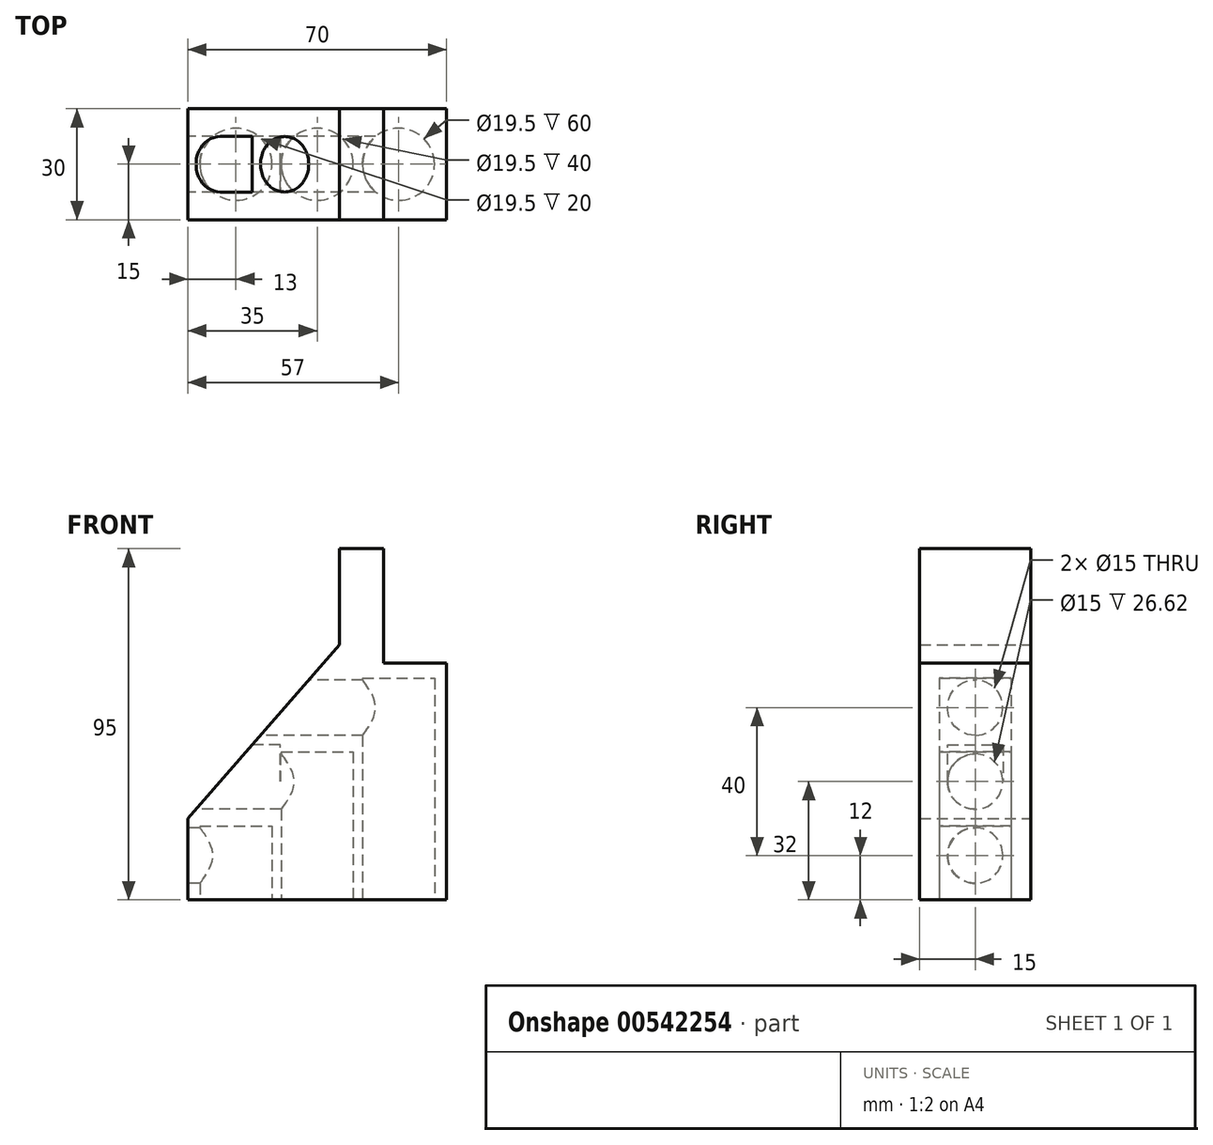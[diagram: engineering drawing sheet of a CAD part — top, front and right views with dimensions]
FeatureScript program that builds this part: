
annotation { "Feature Type Name" : "Feature", "Feature Type Description" : "" }
export const myFeature = defineFeature(function(context is Context, id is Id, definition is map)
    precondition{}
    {
        {
            var Q0;
            Q0=qCreatedBy(makeId("Top.planeOp"),FACE);
            var sketch = newSketch(context, id + "F0", { "sketchPlane" : qUnion([Q0])});
            skLineSegment(sketch, "E0.direction1", {"start": v(0, 0) * mm, "end": v(22, 0) * mm, "construction": true});
            skLineSegment(sketch, "E1.bottom", {"start": v(-13, 15) * mm, "end": v(57, 15) * mm});
            skLineSegment(sketch, "E1.top", {"start": v(-13, -15) * mm, "end": v(57, -15) * mm});
            skLineSegment(sketch, "E1.left", {"start": v(-13, 15) * mm, "end": v(-13, -15) * mm});
            skLineSegment(sketch, "E1.right", {"start": v(57, 15) * mm, "end": v(57, -15) * mm});
            skSolve(sketch);
        }
        {
            var Q0;
            Q0 = qSketchRegion(id + "F0", true);
            var Q1;
            Q1=makeQuery(id+"F0.imprint","IMPRINT",FACE,{"disambiguationData":[TD([[makeQuery(id+"F0.imprint","IMPRINT",EDGE,{"derivedFrom":sQuery(id+"F0.wireOp",EDGE,"SlxlytLZ-BfXm-e8RE-Wzol-MLgFMUTTCqxw")}),1.0]])]});
            var Q2;
            Q2=makeQuery(id+"F0.imprint","IMPRINT",FACE,{"disambiguationData":[TD([[makeQuery(id+"F0.imprint","IMPRINT",EDGE,{"derivedFrom":sQuery(id+"F0.wireOp",EDGE,"E0.1.0.0")}),1.0]])]});
            var Q3;
            Q3=makeQuery(id+"F0.imprint","IMPRINT",FACE,{"disambiguationData":[TD([[makeQuery(id+"F0.imprint","IMPRINT",EDGE,{"derivedFrom":sQuery(id+"F0.wireOp",EDGE,"E0.2.0.0")}),1.0]])]});
            extrude(context, id + "F1", {"entities" : qUnion([Q0, Q1, Q2, Q3]), "depth" : 95 * mm, "offsetDistance" : 25 * mm});
        }
        {
            var Q0;
            Q0=makeQuery(id+"F1.opExtrude","SWEPT_FACE",FACE,{"disambiguationData":[OSD([sQuery(id+"F0.wireOp",EDGE,"E1.top")])]});
            var sketch = newSketch(context, id + "F2", { "sketchPlane" : qUnion([Q0])});
            skLineSegment(sketch, "E2", {"start": v(40, 95) * mm, "end": v(40, 64) * mm});
            skLineSegment(sketch, "E3", {"start": v(40, 64) * mm, "end": v(57, 64) * mm});
            skSolve(sketch);
        }
        {
            var Q0;
            Q0 = qSketchRegion(id + "F2", true);
            var Q1;
            {var subQ0=sQuery(id+"F2.wireOp",EDGE,"E2");Q1=makeQuery(id+"F2.imprint","IMPRINT",FACE,{"disambiguationData":[TD([[makeQuery(id+"F2.imprint","IMPRINT",EDGE,{"derivedFrom":subQ0}),1.0]])]});}
            extrude(context, id + "F3", {"entities" : qUnion([Q0, Q1]), "operationType" : NewBodyOperationType.REMOVE, "oppositeDirection" : true, "depth" : 41.4 * mm, "offsetDistance" : 25 * mm});
        }
        {
            var Q0;
            Q0=makeQuery(id+"F1.opExtrude","CAP_FACE",FACE,{"disambiguationData":[OSD([sQuery(id+"F0.wireOp",EDGE,"E1.bottom"),sQuery(id+"F0.wireOp",EDGE,"E1.top"),sQuery(id+"F0.wireOp",EDGE,"E1.left"),sQuery(id+"F0.wireOp",EDGE,"E1.right")])],"isStart":true});
            var sketch = newSketch(context, id + "F4", { "sketchPlane" : qUnion([Q0])});
            skCircle(sketch, "E4", {"center": v(44, 0) * mm, "radius": 9.75 * mm});
            skSolve(sketch);
        }
        {
            var Q0;
            Q0 = qSketchRegion(id + "F4", true);
            extrude(context, id + "F5", {"entities" : qUnion([Q0]), "operationType" : NewBodyOperationType.REMOVE, "oppositeDirection" : true, "depth" : 60 * mm, "offsetDistance" : 25 * mm});
        }
        {
            var Q0;
            Q0=makeQuery(id+"F1.opExtrude","SWEPT_FACE",FACE,{"disambiguationData":[OSD([sQuery(id+"F0.wireOp",EDGE,"E1.left")])]});
            var sketch = newSketch(context, id + "F6", { "sketchPlane" : qUnion([Q0])});
            skCircle(sketch, "E5", {"center": v(0, 52) * mm, "radius": 7.5 * mm});
            skLineSegment(sketch, "E6", {"start": v(-15, 64) * mm, "end": v(15, 64) * mm, "construction": true});
            skLineSegment(sketch, "E7", {"start": v(-15, 22) * mm, "end": v(15, 22) * mm, "construction": true});
            skCircle(sketch, "E8", {"center": v(0, 32) * mm, "radius": 7.5 * mm, "construction": true});
            skCircle(sketch, "E9", {"center": v(0, 12) * mm, "radius": 7.5 * mm, "construction": true});
            skSolve(sketch);
        }
        {
            var Q0;
            Q0=makeQuery(id+"F1.opExtrude","SWEPT_FACE",FACE,{"disambiguationData":[OSD([sQuery(id+"F0.wireOp",EDGE,"E1.bottom")])]});
            var sketch = newSketch(context, id + "F7", { "sketchPlane" : qUnion([Q0])});
            skLineSegment(sketch, "E10", {"start": v(-28, 95) * mm, "end": v(-28, 69) * mm});
            skLineSegment(sketch, "E11", {"start": v(-28, 69) * mm, "end": v(13, 22) * mm});
            skLineSegment(sketch, "E12", {"start": v(-28, 95) * mm, "end": v(13, 95) * mm});
            skLineSegment(sketch, "E13", {"start": v(13, 95) * mm, "end": v(13, 22) * mm});
            skSolve(sketch);
        }
        {
            var Q0;
            Q0 = qSketchRegion(id + "F7", true);
            extrude(context, id + "F8", {"entities" : qUnion([Q0]), "operationType" : NewBodyOperationType.REMOVE, "oppositeDirection" : true, "depth" : 43.7 * mm, "offsetDistance" : 25 * mm});
        }
        {
            var Q0;
            Q0 = qSketchRegion(id + "F6", true);
            extrude(context, id + "F9", {"entities" : qUnion([Q0]), "operationType" : NewBodyOperationType.REMOVE, "oppositeDirection" : true, "depth" : (70 - 13) * mm, "offsetDistance" : 25 * mm});
        }
        {
            var Q0;
            Q0=makeQuery(id+"F1.opExtrude","CAP_FACE",FACE,{"disambiguationData":[OSD([sQuery(id+"F0.wireOp",EDGE,"E1.bottom"),sQuery(id+"F0.wireOp",EDGE,"E1.top"),sQuery(id+"F0.wireOp",EDGE,"E1.left"),sQuery(id+"F0.wireOp",EDGE,"E1.right")])],"isStart":true});
            var sketch = newSketch(context, id + "F10", { "sketchPlane" : qUnion([Q0])});
            skCircle(sketch, "E14", {"center": v(22, 0) * mm, "radius": 9.75 * mm});
            skCircle(sketch, "E15", {"center": v(44, 0) * mm, "radius": 3.86 * mm, "construction": true});
            skSolve(sketch);
        }
        {
            var Q0;
            Q0 = qSketchRegion(id + "F10", true);
            extrude(context, id + "F11", {"entities" : qUnion([Q0]), "operationType" : NewBodyOperationType.REMOVE, "oppositeDirection" : true, "depth" : 40 * mm, "offsetDistance" : 25 * mm});
        }
        {
            var Q0;
            Q0=makeQuery(id+"F1.opExtrude","CAP_FACE",FACE,{"disambiguationData":[OSD([sQuery(id+"F0.wireOp",EDGE,"E1.bottom"),sQuery(id+"F0.wireOp",EDGE,"E1.top"),sQuery(id+"F0.wireOp",EDGE,"E1.left"),sQuery(id+"F0.wireOp",EDGE,"E1.right")])],"isStart":true});
            var sketch = newSketch(context, id + "F12", { "sketchPlane" : qUnion([Q0])});
            skCircle(sketch, "E16", {"center": v(0, 0) * mm, "radius": 9.75 * mm});
            skSolve(sketch);
        }
        {
            var Q0;
            Q0 = qSketchRegion(id + "F12", true);
            extrude(context, id + "F13", {"entities" : qUnion([Q0]), "operationType" : NewBodyOperationType.REMOVE, "oppositeDirection" : true, "depth" : 20 * mm, "offsetDistance" : 25 * mm});
        }
        {
            var Q0;
            Q0=makeQuery(id+"F1.opExtrude","SWEPT_FACE",FACE,{"disambiguationData":[OSD([sQuery(id+"F0.wireOp",EDGE,"E1.left")])]});
            var sketch = newSketch(context, id + "F14", { "sketchPlane" : qUnion([Q0])});
            skCircle(sketch, "E17", {"center": v(0, 32) * mm, "radius": 7.5 * mm});
            skSolve(sketch);
        }
        {
            var Q0;
            Q0 = qSketchRegion(id + "F14", true);
            extrude(context, id + "F15", {"entities" : qUnion([Q0]), "operationType" : NewBodyOperationType.REMOVE, "oppositeDirection" : true, "depth" : 32.1 * mm, "offsetDistance" : 25 * mm});
        }
        {
            var Q0;
            Q0=makeQuery(id+"F1.opExtrude","SWEPT_FACE",FACE,{"disambiguationData":[OSD([sQuery(id+"F0.wireOp",EDGE,"E1.left")])]});
            var sketch = newSketch(context, id + "F16", { "sketchPlane" : qUnion([Q0])});
            skCircle(sketch, "E18", {"center": v(0, 12) * mm, "radius": 7.5 * mm});
            skSolve(sketch);
        }
        {
            var Q0;
            Q0 = qSketchRegion(id + "F16", true);
            extrude(context, id + "F17", {"entities" : qUnion([Q0]), "operationType" : NewBodyOperationType.REMOVE, "oppositeDirection" : true, "depth" : 11.1 * mm, "offsetDistance" : 25 * mm});
        }
        {
            var Q0;
            Q0=makeQuery(id+"F1.opExtrude","SWEPT_FACE",FACE,{"disambiguationData":[OSD([sQuery(id+"F0.wireOp",EDGE,"E1.left")])]});
            var sketch = newSketch(context, id + "F18", { "sketchPlane" : qUnion([Q0])});
            skLineSegment(sketch, "E19", {"start": v(-7.5, 32) * mm, "end": v(-7.5, 42) * mm});
            skLineSegment(sketch, "E20", {"start": v(-7.5, 42) * mm, "end": v(7.5, 42) * mm});
            skLineSegment(sketch, "E21", {"start": v(7.5, 42) * mm, "end": v(7.5, 32) * mm});
            skArc(sketch, "E22", {"start": v(-7.5, 32) * mm, "mid": v(0, 24.5) * mm, "end": v(7.5, 32) * mm});
            skSolve(sketch);
        }
        {
            var Q0;
            Q0=makeQuery(id+"F18.imprint","IMPRINT",FACE,{"disambiguationData":[TD([[makeQuery(id+"F18.imprint","IMPRINT",EDGE,{"derivedFrom":sQuery(id+"F18.wireOp",EDGE,"E19")}),-1.0]])]});
            extrude(context, id + "F19", {"entities" : qUnion([Q0]), "operationType" : NewBodyOperationType.REMOVE, "oppositeDirection" : true, "depth" : 25 * mm, "offsetDistance" : 25 * mm});
        }
    });
